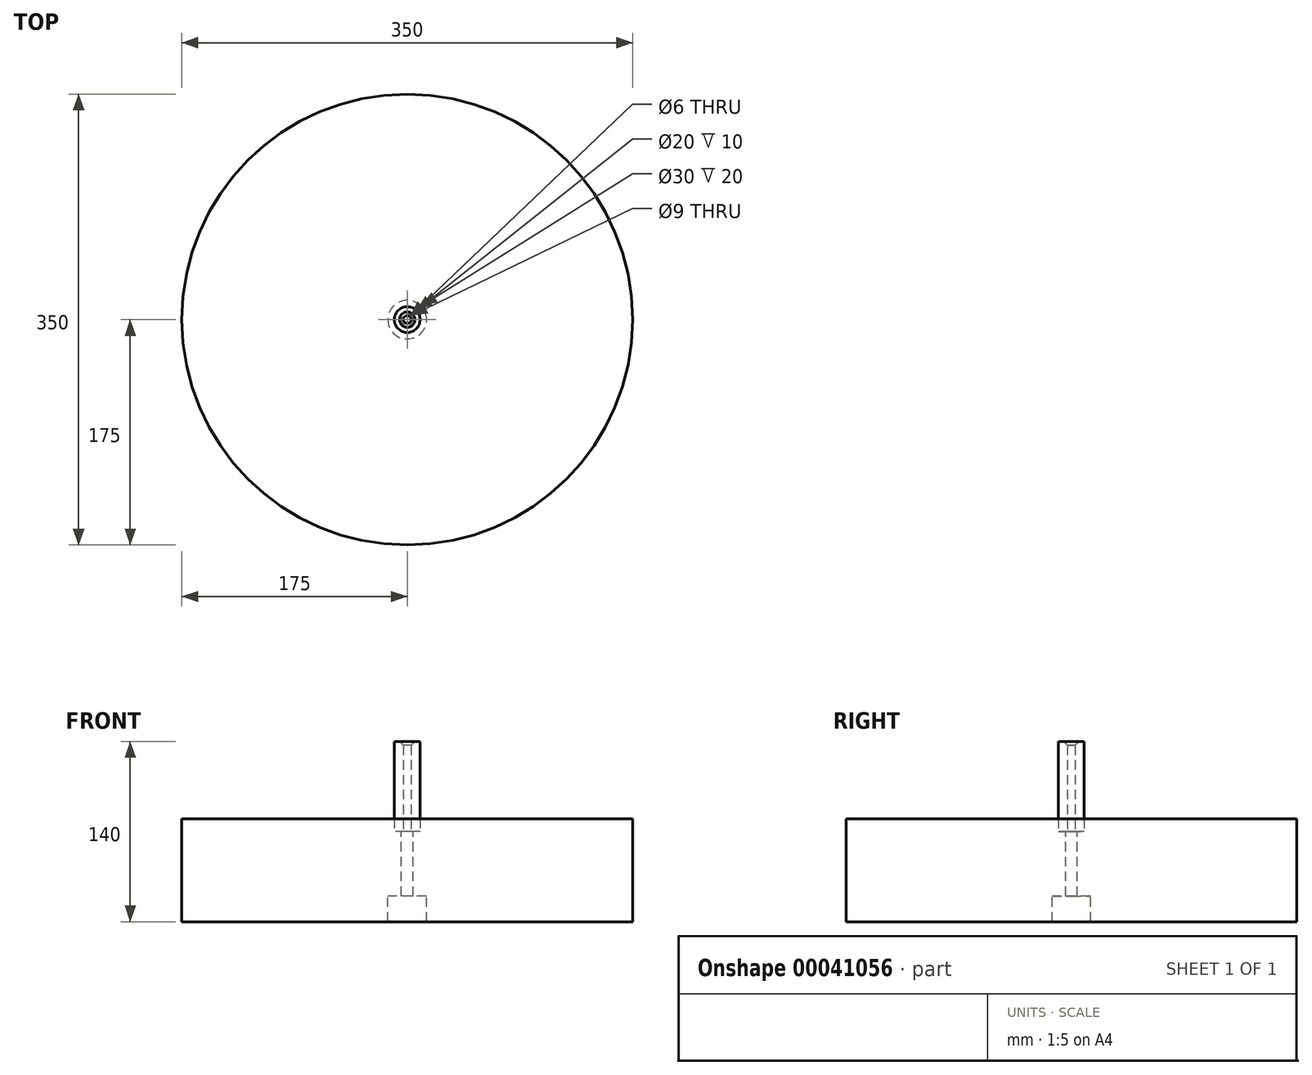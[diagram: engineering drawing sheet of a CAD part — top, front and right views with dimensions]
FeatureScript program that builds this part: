
annotation { "Feature Type Name" : "Feature", "Feature Type Description" : "" }
export const myFeature = defineFeature(function(context is Context, id is Id, definition is map)
    precondition{}
    {
        {
            var Q0;
            Q0=qCreatedBy(makeId("Front.planeOp"),FACE);
            var sketch = newSketch(context, id + "F0", { "sketchPlane" : qUnion([Q0])});
            skLineSegment(sketch, "E0", {"start": v(-10, 13.78) * mm, "end": v(-10, 3.78) * mm});
            skLineSegment(sketch, "E1", {"start": v(-10, 3.78) * mm, "end": v(-4.5, 3.78) * mm});
            skLineSegment(sketch, "E2", {"start": v(-4.5, 3.78) * mm, "end": v(-4.5, -46.22) * mm});
            skLineSegment(sketch, "E3", {"start": v(-4.5, -46.22) * mm, "end": v(-15, -46.22) * mm});
            skLineSegment(sketch, "E4", {"start": v(-15, -46.22) * mm, "end": v(-15, -66.22) * mm});
            skLineSegment(sketch, "E5", {"start": v(-15, -66.22) * mm, "end": v(-175, -66.22) * mm});
            skLineSegment(sketch, "E6", {"start": v(-175, -66.22) * mm, "end": v(-175, 13.78) * mm});
            skLineSegment(sketch, "E7", {"start": v(-175, 13.78) * mm, "end": v(-10, 13.78) * mm});
            skLineSegment(sketch, "E8", {"start": v(0, 135.67) * mm, "end": v(0, -116.17) * mm, "construction": true});
            skSolve(sketch);
        }
        {
            var Q0;
            Q0=makeQuery(id+"F0.imprint","IMPRINT",FACE,{"disambiguationData":[TD([[makeQuery(id+"F0.imprint","IMPRINT",EDGE,{"derivedFrom":sQuery(id+"F0.wireOp",EDGE,"E0")}),-1.0]])]});
            var Q1;
            Q1=sQuery(id+"F0.wireOp",EDGE,"E8");
            revolve(context, id + "F1", {"entities" : qUnion([Q0]), "axis" : qUnion([Q1]), "revolveType" : RevolveType.FULL});
        }
        {
            var Q0;
            Q0=makeQuery(id+"F1.opRevolve","SWEPT_FACE",FACE,{"disambiguationData":[OSD([sQuery(id+"F0.wireOp",EDGE,"E7")])]});
            var sketch = newSketch(context, id + "F2", { "sketchPlane" : qUnion([Q0])});
            skPoint(sketch, "E9.0", {"position": v(0, 0) * mm});
            skCircle(sketch, "E10", {"center": v(0, 0) * mm, "radius": 10 * mm});
            skCircle(sketch, "E11", {"center": v(0, 0) * mm, "radius": 3 * mm});
            skSolve(sketch);
        }
        {
            var Q0;
            Q0=makeQuery(id+"F2.imprint","IMPRINT",FACE,{"disambiguationData":[TD([[makeQuery(id+"F2.imprint","IMPRINT",EDGE,{"derivedFrom":sQuery(id+"F2.wireOp",EDGE,"E10")}),1.0]])]});
            extrude(context, id + "F3", {"entities" : qUnion([Q0]), "depth" : 60 * mm, "hasSecondDirection" : true, "secondDirectionOppositeDirection" : true, "secondDirectionDepth" : 10 * mm});
        }
        {
            var Q0;
            Q0=makeQuery(id+"F3.opExtrude","CAP_EDGE",EDGE,{"disambiguationData":[OSD([sQuery(id+"F2.wireOp",EDGE,"E11")])],"isStart":false});
            chamfer(context, id + "F4", {"entities" : qUnion([Q0]), "width" : 3 * mm, "tangentPropagation" : true});
        }
    });
